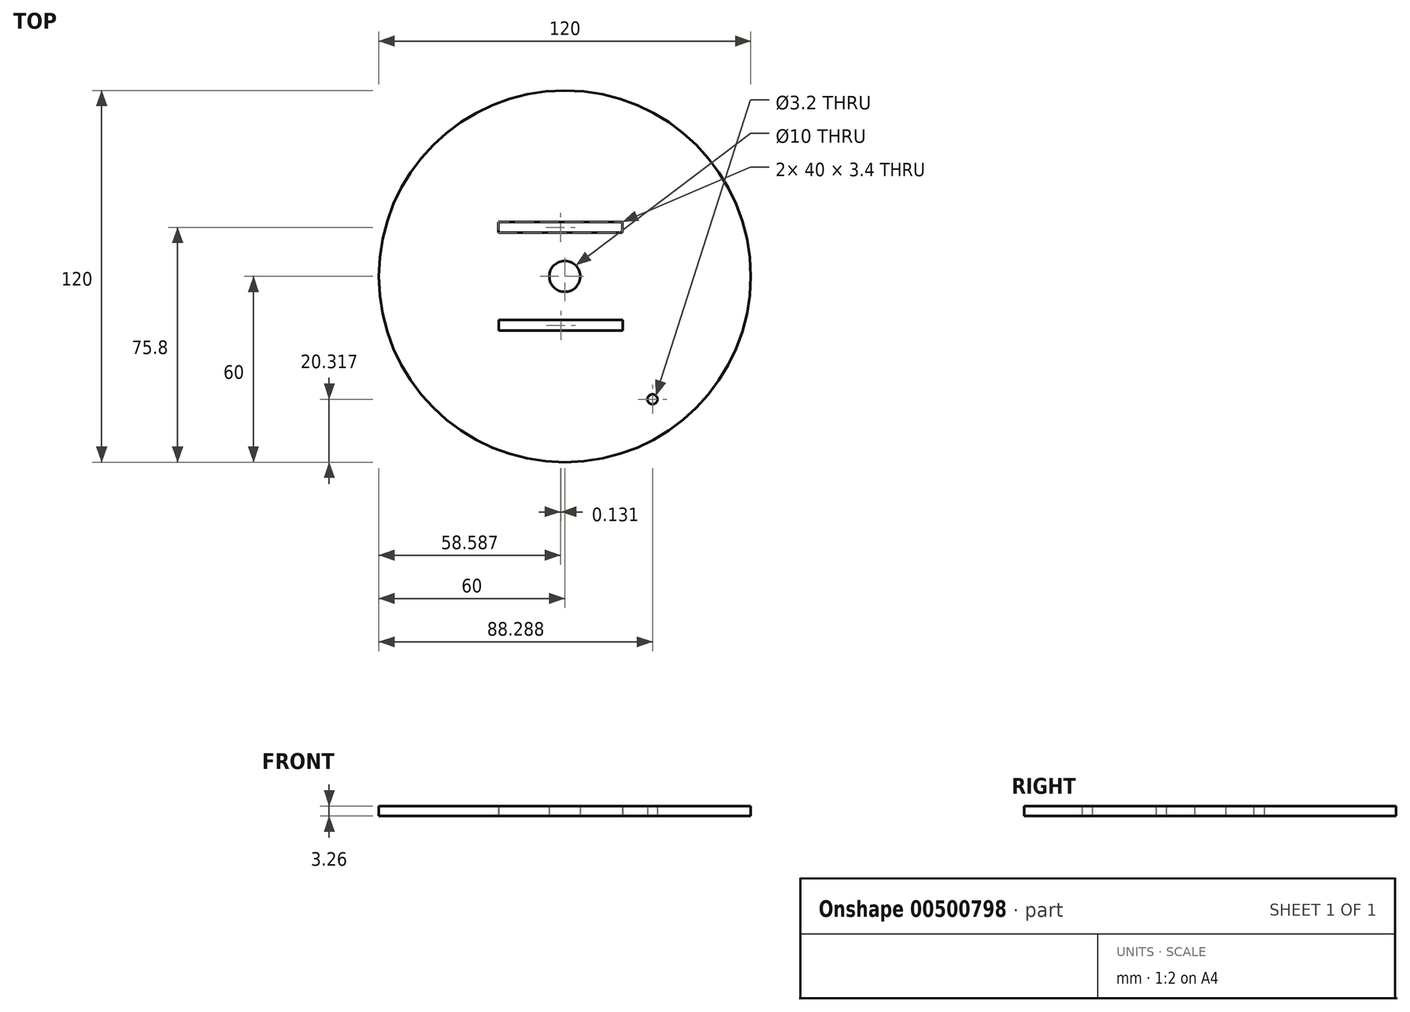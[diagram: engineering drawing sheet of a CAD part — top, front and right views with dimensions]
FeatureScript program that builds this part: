
annotation { "Feature Type Name" : "Feature", "Feature Type Description" : "" }
export const myFeature = defineFeature(function(context is Context, id is Id, definition is map)
    precondition{}
    {
        {
            var Q0;
            Q0=qCreatedBy(makeId("Top.planeOp"),FACE);
            var sketch = newSketch(context, id + "F0", { "sketchPlane" : qUnion([Q0])});
            skCircle(sketch, "E0", {"center": v(0, 0) * mm, "radius": 60 * mm});
            skCircle(sketch, "E1", {"center": v(0, 0) * mm, "radius": 5 * mm});
            skLineSegment(sketch, "E2", {"start": v(0, 0) * mm, "end": v(28.29, -39.68) * mm});
            skCircle(sketch, "E3", {"center": v(28.29, -39.68) * mm, "radius": 1.6 * mm});
            skLineSegment(sketch, "E4", {"start": v(28.29, -39.68) * mm, "end": v(-0.21, -60) * mm});
            skLineSegment(sketch, "E5", {"start": v(0, 5) * mm, "end": v(0, 55) * mm});
            skLineSegment(sketch, "E6", {"start": v(0, -5) * mm, "end": v(0, -55) * mm});
            skLineSegment(sketch, "E7", {"start": v(0, 5) * mm, "end": v(0, 30) * mm});
            skLineSegment(sketch, "E8", {"start": v(0, -5) * mm, "end": v(0, -30) * mm});
            skLineSegment(sketch, "E9", {"start": v(0, 5) * mm, "end": v(0, 17.5) * mm});
            skLineSegment(sketch, "E10", {"start": v(-21.28, -17.5) * mm, "end": v(18.72, -17.5) * mm});
            skLineSegment(sketch, "E11", {"start": v(18.72, -17.5) * mm, "end": v(18.72, -14.1) * mm});
            skLineSegment(sketch, "E12", {"start": v(-21.28, -17.5) * mm, "end": v(-21.28, -14.1) * mm});
            skLineSegment(sketch, "E13", {"start": v(-21.28, -14.1) * mm, "end": v(18.72, -14.1) * mm});
            skLineSegment(sketch, "E14", {"start": v(-21.41, 17.5) * mm, "end": v(18.59, 17.5) * mm});
            skLineSegment(sketch, "E15", {"start": v(-21.41, 17.5) * mm, "end": v(-21.41, 14.1) * mm});
            skLineSegment(sketch, "E16", {"start": v(18.59, 17.5) * mm, "end": v(18.59, 14.1) * mm});
            skLineSegment(sketch, "E17", {"start": v(18.59, 14.1) * mm, "end": v(-21.41, 14.1) * mm});
            skLineSegment(sketch, "E18", {"start": v(-11.03, 14.1) * mm, "end": v(-11.03, -14.1) * mm});
            skSolve(sketch);
        }
        {
            var Q0;
            Q0 = qSketchRegion(id + "F0", true);
            var Q1;
            {var subQ0=sQuery(id+"F0.wireOp",EDGE,"jZ4vb3YU-sxm1-G6jN-Z3zV-Bo199GurXkQQ");var subQ1=sQuery(id+"F0.wireOp",EDGE,"E1");var subQ2=makeQuery(id+"F0.imprint","INTERSECT",VERTEX,{"derivedFrom":[subQ1,subQ0]});Q1=makeQuery(id+"F0.imprint","IMPRINT",FACE,{"disambiguationData":[TD([[makeQuery(id+"F0.imprint","IMPRINT",EDGE,{"disambiguationData":[TD([[subQ2,-1.0]])],"derivedFrom":subQ1}),-1.0]])]});}
            var Q2;
            {var subQ7=sQuery(id+"F0.wireOp",EDGE,"E18");Q2=makeQuery(id+"F0.imprint","IMPRINT",FACE,{"disambiguationData":[TD([[makeQuery(id+"F0.imprint","IMPRINT",EDGE,{"derivedFrom":subQ7}),1.0]])]});}
            extrude(context, id + "F1", {"entities" : qUnion([Q0, Q1, Q2]), "depth" : 3.25 * mm, "offsetDistance" : 25 * mm, "symmetric" : true});
        }
    });
